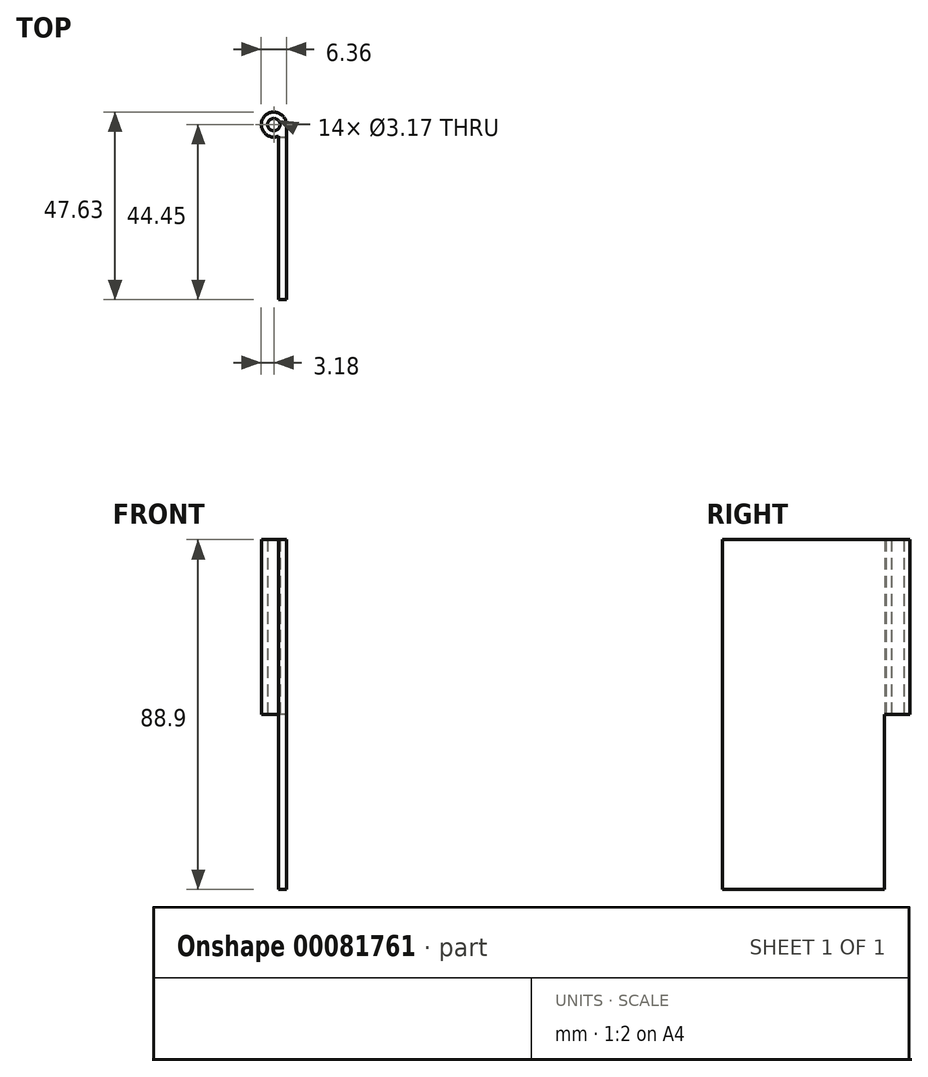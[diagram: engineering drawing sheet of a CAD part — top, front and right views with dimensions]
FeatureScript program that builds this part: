
annotation { "Feature Type Name" : "Feature", "Feature Type Description" : "" }
export const myFeature = defineFeature(function(context is Context, id is Id, definition is map)
    precondition{}
    {
        {
            var Q0;
            Q0=qCreatedBy(makeId("Top.planeOp"),FACE);
            var sketch = newSketch(context, id + "F0", { "sketchPlane" : qUnion([Q0])});
            skArc(sketch, "E0", {"start": v(3.18, 0) * mm, "mid": v(-2.62, 1.8) * mm, "end": v(1.14, -2.96) * mm});
            skCircle(sketch, "E1", {"center": v(0, 0) * mm, "radius": 1.59 * mm});
            skLineSegment(sketch, "E2", {"start": v(3.18, 0) * mm, "end": v(3.18, -44.45) * mm});
            skLineSegment(sketch, "E3", {"start": v(3.18, -44.45) * mm, "end": v(1.14, -44.45) * mm});
            skLineSegment(sketch, "E4", {"start": v(1.14, -44.45) * mm, "end": v(1.14, -2.96) * mm});
            skSolve(sketch);
        }
        {
            var Q0;
            Q0 = qSketchRegion(id + "F0", true);
            extrude(context, id + "F1", {"entities" : qUnion([Q0]), "depth" : 88.9 * mm});
        }
        {
            var Q0;
            Q0=makeQuery(id+"F1.opExtrude","SWEPT_FACE",FACE,{"disambiguationData":[OSD([sQuery(id+"F0.wireOp",EDGE,"E4")])]});
            var sketch = newSketch(context, id + "F2", { "sketchPlane" : qUnion([Q0])});
            skLineSegment(sketch, "E5.bottom", {"start": v(3.3, 0) * mm, "end": v(-12.37, 0) * mm});
            skLineSegment(sketch, "E5.top", {"start": v(3.3, 44.45) * mm, "end": v(-12.37, 44.45) * mm});
            skLineSegment(sketch, "E5.left", {"start": v(3.3, 0) * mm, "end": v(3.3, 44.45) * mm});
            skLineSegment(sketch, "E5.right", {"start": v(-12.37, 0) * mm, "end": v(-12.37, 44.45) * mm});
            skSolve(sketch);
        }
        {
            var Q0;
            Q0 = qSketchRegion(id + "F2", true);
            extrude(context, id + "F3", {"entities" : qUnion([Q0]), "operationType" : NewBodyOperationType.REMOVE, "endBound" : BoundingType.SYMMETRIC, "oppositeDirection" : true, "depth" : 25.4 * mm});
        }
    });
